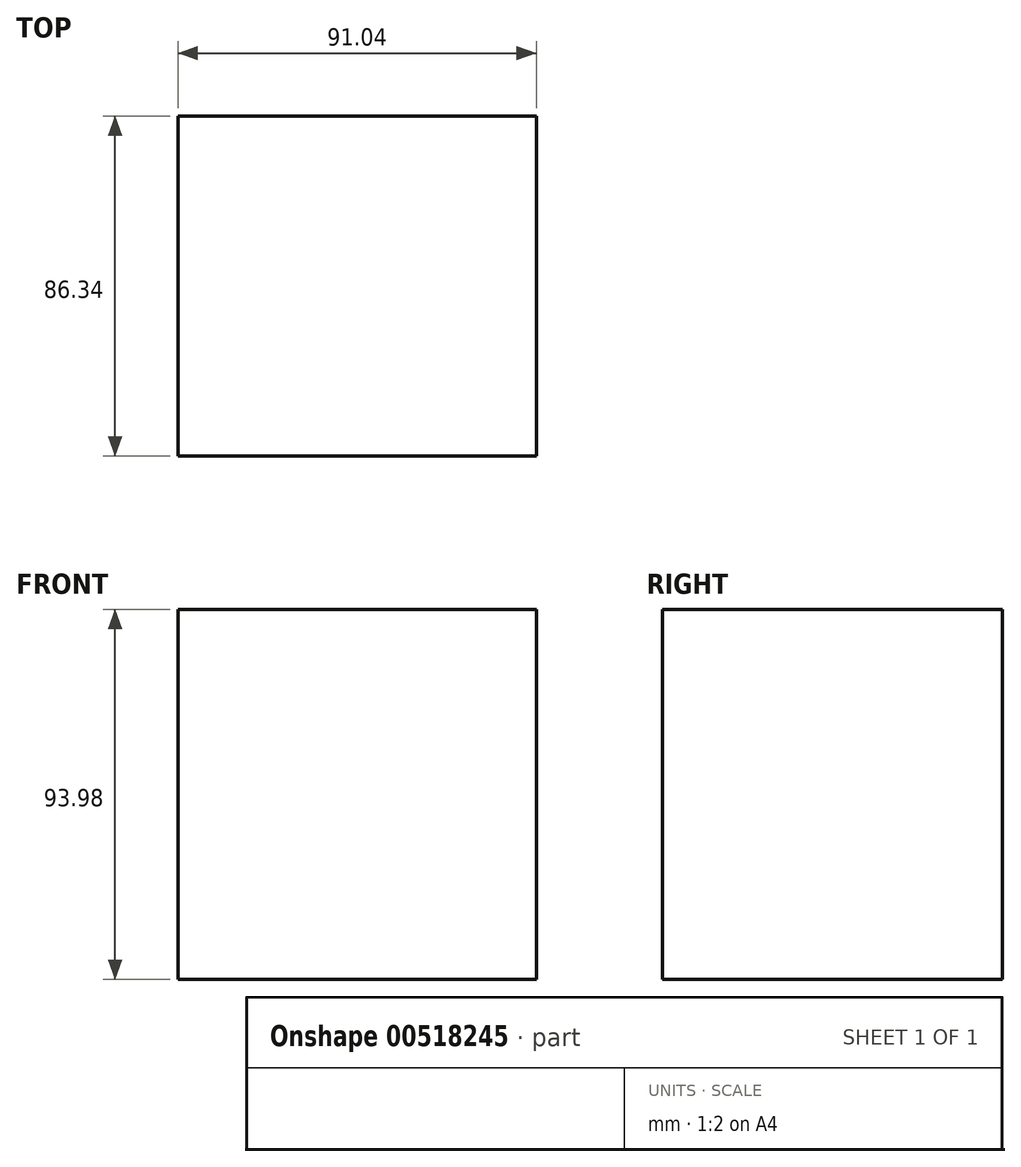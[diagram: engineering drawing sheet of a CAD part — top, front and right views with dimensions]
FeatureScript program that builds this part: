
annotation { "Feature Type Name" : "Feature", "Feature Type Description" : "" }
export const myFeature = defineFeature(function(context is Context, id is Id, definition is map)
    precondition{}
    {
        {
            var Q0;
            Q0=qCreatedBy(makeId("Top.planeOp"),FACE);
            var sketch = newSketch(context, id + "F0", { "sketchPlane" : qUnion([Q0])});
            skLineSegment(sketch, "E0.bottom", {"start": v(45.52, -43.17) * mm, "end": v(-45.52, -43.17) * mm});
            skLineSegment(sketch, "E0.top", {"start": v(45.52, 43.17) * mm, "end": v(-45.52, 43.17) * mm});
            skLineSegment(sketch, "E0.left", {"start": v(45.52, -43.17) * mm, "end": v(45.52, 43.17) * mm});
            skLineSegment(sketch, "E0.right", {"start": v(-45.52, -43.17) * mm, "end": v(-45.52, 43.17) * mm});
            skPoint(sketch, "E0.middle", {"position": v(0, 0) * mm});
            skSolve(sketch);
        }
        {
            var Q0;
            Q0=makeQuery(id+"F0.imprint","IMPRINT",FACE,{"disambiguationData":[TD([[makeQuery(id+"F0.imprint","IMPRINT",EDGE,{"derivedFrom":sQuery(id+"F0.wireOp",EDGE,"E0.bottom")}),-1.0]])]});
            extrude(context, id + "F1", {"entities" : qUnion([Q0]), "depth" : 93.98 * mm, "offsetDistance" : 25.4 * mm});
        }
    });
